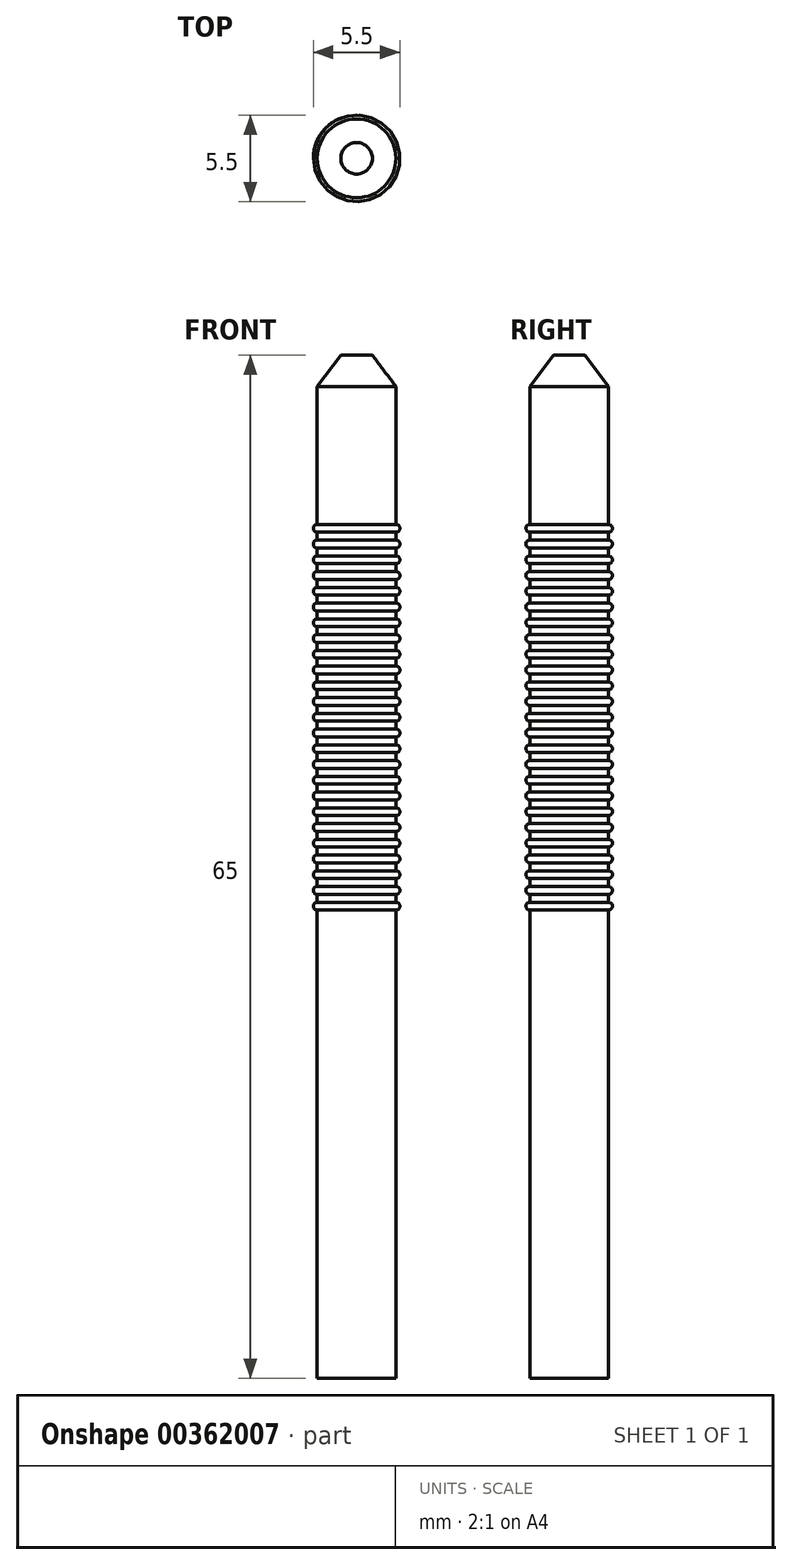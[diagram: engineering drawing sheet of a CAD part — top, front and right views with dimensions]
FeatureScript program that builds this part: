
annotation { "Feature Type Name" : "Feature", "Feature Type Description" : "" }
export const myFeature = defineFeature(function(context is Context, id is Id, definition is map)
    precondition{}
    {
        {
            var Q0;
            Q0=qCreatedBy(makeId("Top.planeOp"),FACE);
            var sketch = newSketch(context, id + "F0", { "sketchPlane" : qUnion([Q0])});
            skCircle(sketch, "E0", {"center": v(0, 0) * mm, "radius": 2.5 * mm});
            skSolve(sketch);
        }
        {
            var Q0;
            Q0 = qSketchRegion(id + "F0", true);
            extrude(context, id + "F1", {"entities" : qUnion([Q0]), "depth" : 65 * mm});
        }
        {
            var Q0;
            Q0=qCreatedBy(makeId("Front.planeOp"),FACE);
            var sketch = newSketch(context, id + "F2", { "sketchPlane" : qUnion([Q0])});
            skArc(sketch, "E1", {"start": v(2.5, 29.75) * mm, "mid": v(2.75, 30) * mm, "end": v(2.5, 30.25) * mm});
            skLineSegment(sketch, "E2", {"start": v(2.5, 30.25) * mm, "end": v(2.5, 29.75) * mm});
            skArc(sketch, "E3.0.1.0", {"start": v(2.5, 30.75) * mm, "mid": v(2.75, 31) * mm, "end": v(2.5, 31.25) * mm});
            skLineSegment(sketch, "E3.0.1.1", {"start": v(2.5, 31.25) * mm, "end": v(2.5, 30.75) * mm});
            skArc(sketch, "E3.0.2.0", {"start": v(2.5, 31.75) * mm, "mid": v(2.75, 32) * mm, "end": v(2.5, 32.25) * mm});
            skLineSegment(sketch, "E3.0.2.1", {"start": v(2.5, 32.25) * mm, "end": v(2.5, 31.75) * mm});
            skArc(sketch, "E3.0.3.0", {"start": v(2.5, 32.75) * mm, "mid": v(2.75, 33) * mm, "end": v(2.5, 33.25) * mm});
            skLineSegment(sketch, "E3.0.3.1", {"start": v(2.5, 33.25) * mm, "end": v(2.5, 32.75) * mm});
            skArc(sketch, "E3.0.4.0", {"start": v(2.5, 33.75) * mm, "mid": v(2.75, 34) * mm, "end": v(2.5, 34.25) * mm});
            skLineSegment(sketch, "E3.0.4.1", {"start": v(2.5, 34.25) * mm, "end": v(2.5, 33.75) * mm});
            skArc(sketch, "E3.0.5.0", {"start": v(2.5, 34.75) * mm, "mid": v(2.75, 35) * mm, "end": v(2.5, 35.25) * mm});
            skLineSegment(sketch, "E3.0.5.1", {"start": v(2.5, 35.25) * mm, "end": v(2.5, 34.75) * mm});
            skArc(sketch, "E3.0.6.0", {"start": v(2.5, 35.75) * mm, "mid": v(2.75, 36) * mm, "end": v(2.5, 36.25) * mm});
            skLineSegment(sketch, "E3.0.6.1", {"start": v(2.5, 36.25) * mm, "end": v(2.5, 35.75) * mm});
            skArc(sketch, "E3.0.7.0", {"start": v(2.5, 36.75) * mm, "mid": v(2.75, 37) * mm, "end": v(2.5, 37.25) * mm});
            skLineSegment(sketch, "E3.0.7.1", {"start": v(2.5, 37.25) * mm, "end": v(2.5, 36.75) * mm});
            skArc(sketch, "E3.0.8.0", {"start": v(2.5, 37.75) * mm, "mid": v(2.75, 38) * mm, "end": v(2.5, 38.25) * mm});
            skLineSegment(sketch, "E3.0.8.1", {"start": v(2.5, 38.25) * mm, "end": v(2.5, 37.75) * mm});
            skArc(sketch, "E3.0.9.0", {"start": v(2.5, 38.75) * mm, "mid": v(2.75, 39) * mm, "end": v(2.5, 39.25) * mm});
            skLineSegment(sketch, "E3.0.9.1", {"start": v(2.5, 39.25) * mm, "end": v(2.5, 38.75) * mm});
            skArc(sketch, "E3.0.10.0", {"start": v(2.5, 39.75) * mm, "mid": v(2.75, 40) * mm, "end": v(2.5, 40.25) * mm});
            skLineSegment(sketch, "E3.0.10.1", {"start": v(2.5, 40.25) * mm, "end": v(2.5, 39.75) * mm});
            skArc(sketch, "E3.0.11.0", {"start": v(2.5, 40.75) * mm, "mid": v(2.75, 41) * mm, "end": v(2.5, 41.25) * mm});
            skLineSegment(sketch, "E3.0.11.1", {"start": v(2.5, 41.25) * mm, "end": v(2.5, 40.75) * mm});
            skArc(sketch, "E3.0.12.0", {"start": v(2.5, 41.75) * mm, "mid": v(2.75, 42) * mm, "end": v(2.5, 42.25) * mm});
            skLineSegment(sketch, "E3.0.12.1", {"start": v(2.5, 42.25) * mm, "end": v(2.5, 41.75) * mm});
            skArc(sketch, "E3.0.13.0", {"start": v(2.5, 42.75) * mm, "mid": v(2.75, 43) * mm, "end": v(2.5, 43.25) * mm});
            skLineSegment(sketch, "E3.0.13.1", {"start": v(2.5, 43.25) * mm, "end": v(2.5, 42.75) * mm});
            skArc(sketch, "E3.0.14.0", {"start": v(2.5, 43.75) * mm, "mid": v(2.75, 44) * mm, "end": v(2.5, 44.25) * mm});
            skLineSegment(sketch, "E3.0.14.1", {"start": v(2.5, 44.25) * mm, "end": v(2.5, 43.75) * mm});
            skArc(sketch, "E3.0.15.0", {"start": v(2.5, 44.75) * mm, "mid": v(2.75, 45) * mm, "end": v(2.5, 45.25) * mm});
            skLineSegment(sketch, "E3.0.15.1", {"start": v(2.5, 45.25) * mm, "end": v(2.5, 44.75) * mm});
            skArc(sketch, "E3.0.16.0", {"start": v(2.5, 45.75) * mm, "mid": v(2.75, 46) * mm, "end": v(2.5, 46.25) * mm});
            skLineSegment(sketch, "E3.0.16.1", {"start": v(2.5, 46.25) * mm, "end": v(2.5, 45.75) * mm});
            skArc(sketch, "E3.0.17.0", {"start": v(2.5, 46.75) * mm, "mid": v(2.75, 47) * mm, "end": v(2.5, 47.25) * mm});
            skLineSegment(sketch, "E3.0.17.1", {"start": v(2.5, 47.25) * mm, "end": v(2.5, 46.75) * mm});
            skArc(sketch, "E3.0.18.0", {"start": v(2.5, 47.75) * mm, "mid": v(2.75, 48) * mm, "end": v(2.5, 48.25) * mm});
            skLineSegment(sketch, "E3.0.18.1", {"start": v(2.5, 48.25) * mm, "end": v(2.5, 47.75) * mm});
            skArc(sketch, "E3.0.19.0", {"start": v(2.5, 48.75) * mm, "mid": v(2.75, 49) * mm, "end": v(2.5, 49.25) * mm});
            skLineSegment(sketch, "E3.0.19.1", {"start": v(2.5, 49.25) * mm, "end": v(2.5, 48.75) * mm});
            skArc(sketch, "E3.0.20.0", {"start": v(2.5, 49.75) * mm, "mid": v(2.75, 50) * mm, "end": v(2.5, 50.25) * mm});
            skLineSegment(sketch, "E3.0.20.1", {"start": v(2.5, 50.25) * mm, "end": v(2.5, 49.75) * mm});
            skArc(sketch, "E3.0.21.0", {"start": v(2.5, 50.75) * mm, "mid": v(2.75, 51) * mm, "end": v(2.5, 51.25) * mm});
            skLineSegment(sketch, "E3.0.21.1", {"start": v(2.5, 51.25) * mm, "end": v(2.5, 50.75) * mm});
            skArc(sketch, "E3.0.22.0", {"start": v(2.5, 51.75) * mm, "mid": v(2.75, 52) * mm, "end": v(2.5, 52.25) * mm});
            skLineSegment(sketch, "E3.0.22.1", {"start": v(2.5, 52.25) * mm, "end": v(2.5, 51.75) * mm});
            skArc(sketch, "E3.0.23.0", {"start": v(2.5, 52.75) * mm, "mid": v(2.75, 53) * mm, "end": v(2.5, 53.25) * mm});
            skLineSegment(sketch, "E3.0.23.1", {"start": v(2.5, 53.25) * mm, "end": v(2.5, 52.75) * mm});
            skArc(sketch, "E3.0.24.0", {"start": v(2.5, 53.75) * mm, "mid": v(2.75, 54) * mm, "end": v(2.5, 54.25) * mm});
            skLineSegment(sketch, "E3.0.24.1", {"start": v(2.5, 54.25) * mm, "end": v(2.5, 53.75) * mm});
            skLineSegment(sketch, "E3.direction1", {"start": v(2.5, 29.75) * mm, "end": v(27.5, 29.75) * mm, "construction": true});
            skLineSegment(sketch, "E3.direction2", {"start": v(2.5, 29.75) * mm, "end": v(2.5, 30.75) * mm, "construction": true});
            skLineSegment(sketch, "E4", {"start": v(0, 0) * mm, "end": v(0, 59.82) * mm, "construction": true});
            skSolve(sketch);
        }
        {
            var Q0;
            Q0 = qSketchRegion(id + "F2", true);
            var Q1;
            Q1=sQuery(id+"F2.wireOp",EDGE,"E4");
            revolve(context, id + "F3", {"operationType" : NewBodyOperationType.ADD, "entities" : qUnion([Q0]), "axis" : qUnion([Q1]), "revolveType" : RevolveType.FULL});
        }
        {
            var Q0;
            Q0=makeQuery(id+"F1.opExtrude","CAP_EDGE",EDGE,{"disambiguationData":[OSD([sQuery(id+"F0.wireOp",EDGE,"E0")])],"isStart":false});
            chamfer(context, id + "F4", {"entities" : qUnion([Q0]), "chamferType" : ChamferType.TWO_OFFSETS, "width1" : 1.5 * mm, "oppositeDirection" : false, "width2" : 2 * mm, "tangentPropagation" : true});
        }
    });
